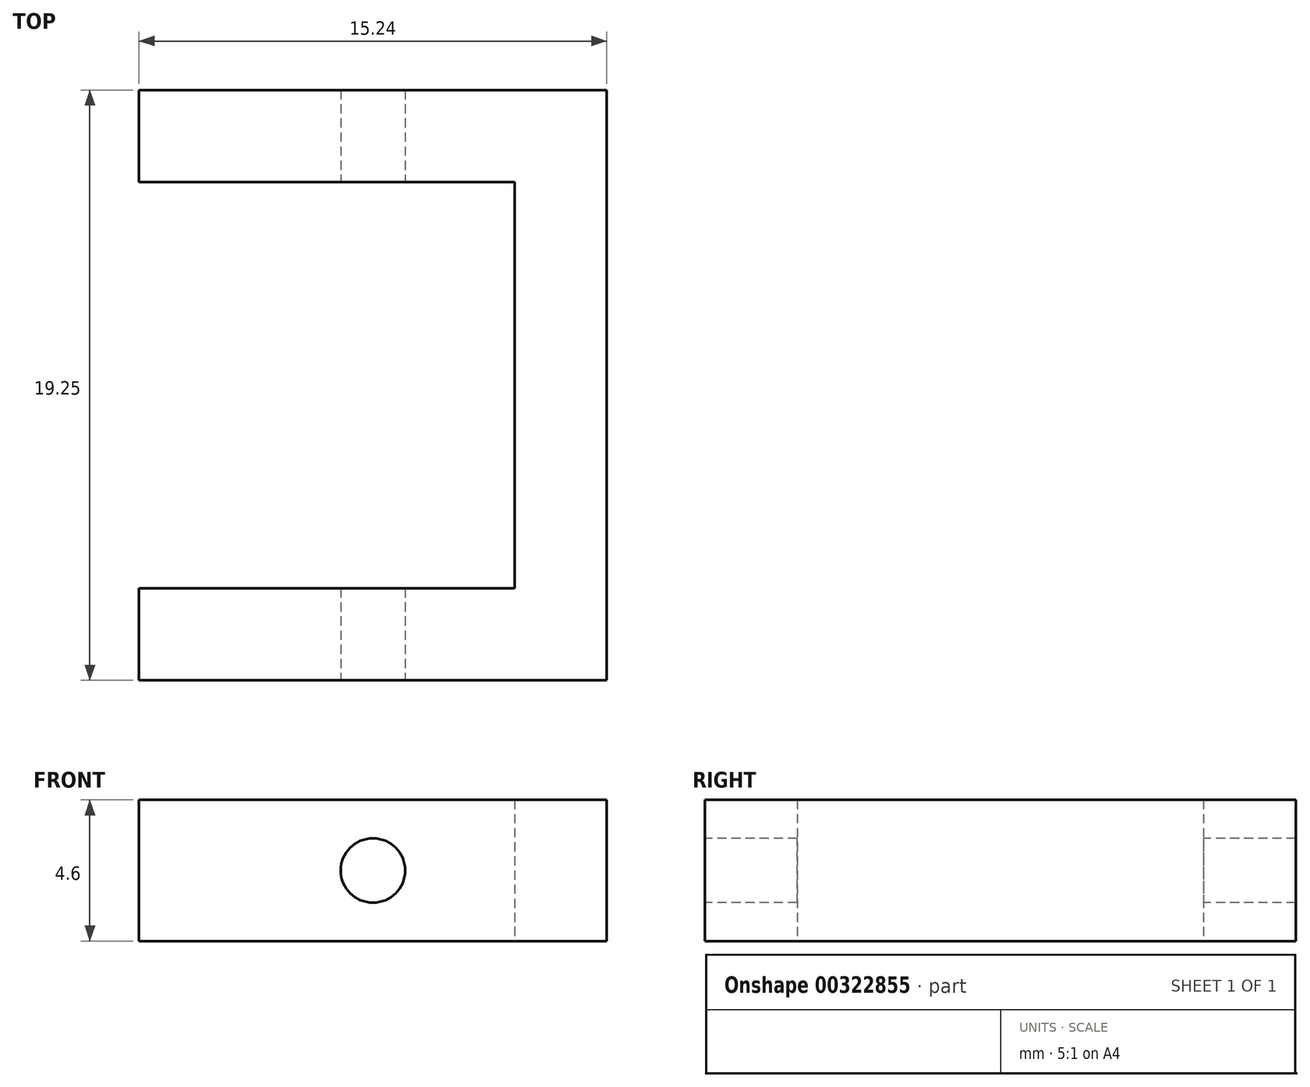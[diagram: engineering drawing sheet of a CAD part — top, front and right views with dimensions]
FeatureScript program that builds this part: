
annotation { "Feature Type Name" : "Feature", "Feature Type Description" : "" }
export const myFeature = defineFeature(function(context is Context, id is Id, definition is map)
    precondition{}
    {
        {
            var Q0;
            Q0=qCreatedBy(makeId("Top.planeOp"),FACE);
            var sketch = newSketch(context, id + "F0", { "sketchPlane" : qUnion([Q0])});
            skLineSegment(sketch, "E0", {"start": v(0, 0) * mm, "end": v(0, 19.25) * mm});
            skLineSegment(sketch, "E1", {"start": v(0, 19.25) * mm, "end": v(-15.24, 19.25) * mm});
            skLineSegment(sketch, "E2", {"start": v(-15.24, 19.25) * mm, "end": v(-15.24, 16.25) * mm});
            skLineSegment(sketch, "E3", {"start": v(-15.24, 16.25) * mm, "end": v(-3, 16.25) * mm});
            skLineSegment(sketch, "E4", {"start": v(-3, 16.25) * mm, "end": v(-3, 3) * mm});
            skLineSegment(sketch, "E5", {"start": v(-3, 3) * mm, "end": v(-15.24, 3) * mm});
            skLineSegment(sketch, "E6", {"start": v(-15.24, 3) * mm, "end": v(-15.24, 0) * mm});
            skLineSegment(sketch, "E7", {"start": v(-15.24, 0) * mm, "end": v(0, 0) * mm});
            skSolve(sketch);
        }
        {
            var Q0;
            Q0 = qSketchRegion(id + "F0", true);
            extrude(context, id + "F1", {"entities" : qUnion([Q0]), "depth" : 4.6 * mm});
        }
        {
            var Q0;
            Q0=makeQuery(id+"F1.opExtrude","SWEPT_FACE",FACE,{"disambiguationData":[OSD([sQuery(id+"F0.wireOp",EDGE,"E7")])]});
            var sketch = newSketch(context, id + "F2", { "sketchPlane" : qUnion([Q0])});
            skCircle(sketch, "E8", {"center": v(-7.62, 2.3) * mm, "radius": 1.05 * mm});
            skPoint(sketch, "E9.orphan", {"position": v(-7.62, 4.6) * mm});
            skPoint(sketch, "E10.start.orphan", {"position": v(-7.62, 0) * mm});
            skSolve(sketch);
        }
        {
            var Q0;
            Q0 = qSketchRegion(id + "F2", true);
            extrude(context, id + "F3", {"entities" : qUnion([Q0]), "operationType" : NewBodyOperationType.REMOVE, "oppositeDirection" : true, "depth" : 25 * mm});
        }
    });
